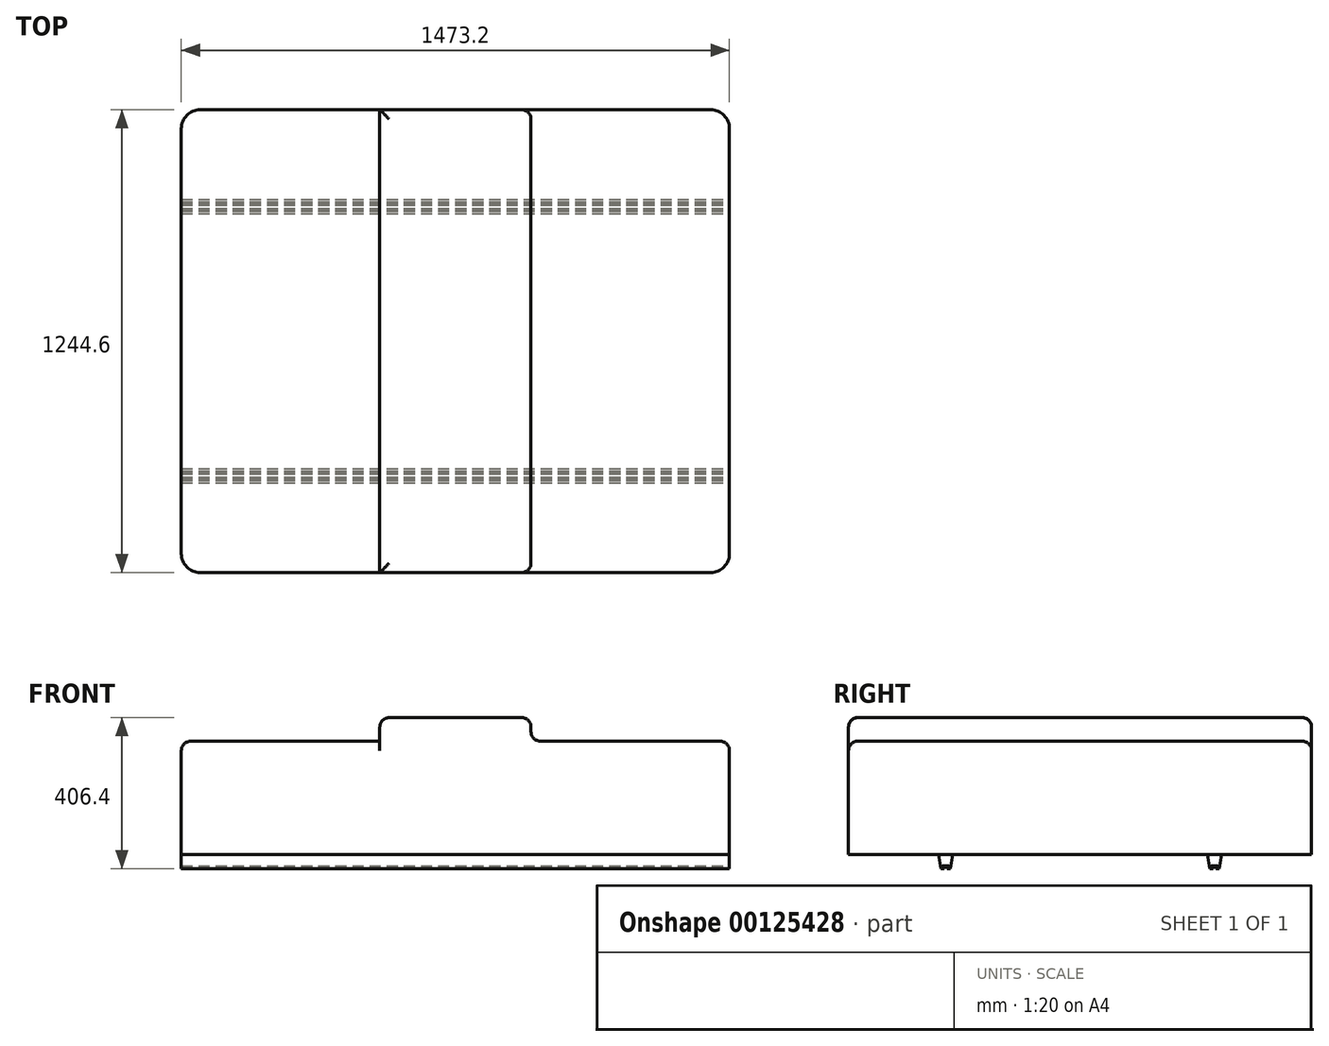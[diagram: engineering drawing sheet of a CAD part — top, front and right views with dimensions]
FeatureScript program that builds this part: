
annotation { "Feature Type Name" : "Feature", "Feature Type Description" : "" }
export const myFeature = defineFeature(function(context is Context, id is Id, definition is map)
    precondition{}
    {
        {
            var Q0;
            Q0=qCreatedBy(makeId("Top.planeOp"),FACE);
            var sketch = newSketch(context, id + "F0", { "sketchPlane" : qUnion([Q0])});
            skLineSegment(sketch, "E0.bottom", {"start": v(-736.6, -622.3) * mm, "end": v(736.6, -622.3) * mm});
            skLineSegment(sketch, "E0.top", {"start": v(-736.6, 622.3) * mm, "end": v(736.6, 622.3) * mm});
            skLineSegment(sketch, "E0.left", {"start": v(-736.6, -622.3) * mm, "end": v(-736.6, 622.3) * mm});
            skLineSegment(sketch, "E0.right", {"start": v(736.6, -622.3) * mm, "end": v(736.6, 622.3) * mm});
            skPoint(sketch, "E0.middle", {"position": v(0, 0) * mm});
            skSolve(sketch);
        }
        {
            var Q0;
            Q0 = qSketchRegion(id + "F0", true);
            var Q1;
            Q1=makeQuery(id+"F0.imprint","IMPRINT",FACE,{"disambiguationData":[TD([[makeQuery(id+"F0.imprint","IMPRINT",EDGE,{"derivedFrom":sQuery(id+"F0.wireOp",EDGE,"E0.bottom")}),1.0]])]});
            extrude(context, id + "F1", {"entities" : qUnion([Q0, Q1]), "depth" : 304.8 * mm});
        }
        {
            var Q0;
            Q0=makeQuery(id+"F1.opExtrude","CAP_FACE",FACE,{"disambiguationData":[OSD([sQuery(id+"F0.wireOp",EDGE,"E0.bottom"),sQuery(id+"F0.wireOp",EDGE,"E0.top"),sQuery(id+"F0.wireOp",EDGE,"E0.left"),sQuery(id+"F0.wireOp",EDGE,"E0.right")])],"isStart":false});
            var sketch = newSketch(context, id + "F2", { "sketchPlane" : qUnion([Q0])});
            skLineSegment(sketch, "E1", {"start": v(0, 622.3) * mm, "end": v(0, -622.3) * mm, "construction": true});
            skLineSegment(sketch, "E2.bottom", {"start": v(-203.2, 622.3) * mm, "end": v(203.2, 622.3) * mm});
            skLineSegment(sketch, "E2.top", {"start": v(-203.2, -622.3) * mm, "end": v(203.2, -622.3) * mm});
            skLineSegment(sketch, "E2.left", {"start": v(-203.2, 622.3) * mm, "end": v(-203.2, -622.3) * mm});
            skLineSegment(sketch, "E2.right", {"start": v(203.2, 622.3) * mm, "end": v(203.2, -622.3) * mm});
            skSolve(sketch);
        }
        {
            var Q0;
            Q0 = qSketchRegion(id + "F2", true);
            extrude(context, id + "F3", {"entities" : qUnion([Q0]), "operationType" : NewBodyOperationType.ADD, "depth" : 63.5 * mm});
        }
        {
            var Q0;
            Q0=makeQuery(id+"F3.opExtrude","CAP_EDGE",EDGE,{"disambiguationData":[OSD([sQuery(id+"F2.wireOp",EDGE,"E2.left")])],"isStart":true});
            var Q1;
            Q1=makeQuery(id+"F3.opExtrude","CAP_EDGE",EDGE,{"disambiguationData":[OSD([sQuery(id+"F2.wireOp",EDGE,"E2.left")])],"isStart":false});
            var Q2;
            Q2=makeQuery(id+"F3.opExtrude","CAP_EDGE",EDGE,{"disambiguationData":[OSD([sQuery(id+"F2.wireOp",EDGE,"E2.right")])],"isStart":false});
            var Q3;
            Q3=makeQuery(id+"F3.opExtrude","CAP_EDGE",EDGE,{"disambiguationData":[OSD([sQuery(id+"F2.wireOp",EDGE,"E2.right")])],"isStart":true});
            var Q4;
            Q4=makeQuery(id+"F3.opExtrude","CAP_EDGE",EDGE,{"disambiguationData":[OSD([sQuery(id+"F2.wireOp",EDGE,"E2.top")])],"isStart":false});
            var Q5;
            Q5=makeQuery(id+"F3.opExtrude","CAP_EDGE",EDGE,{"disambiguationData":[OSD([sQuery(id+"F2.wireOp",EDGE,"E2.bottom")])],"isStart":false});
            fillet(context, id + "F4", {"entities" : qUnion([Q0, Q1, Q2, Q3, Q4, Q5]), "radius" : 25.4 * mm, "tangentPropagation" : true, "allowEdgeOverflow" : false});
        }
        {
            var Q0;
            {var subQ0=sQuery(id+"F0.wireOp",EDGE,"E0.left");var subQ1=sQuery(id+"F0.wireOp",EDGE,"E0.bottom");Q0=makeQuery(id+"F3.boolean.opBoolean","SPLIT",EDGE,{"disambiguationData":[TD([makeQuery(id+"F1.opExtrude","SWEPT_FACE",FACE,{"disambiguationData":[OSD([subQ0])]})])],"derivedFrom":makeQuery(id+"F1.opExtrude","CAP_EDGE",EDGE,{"disambiguationData":[OSD([subQ1])],"isStart":false})});}
            var Q1;
            {var subQ0=sQuery(id+"F0.wireOp",EDGE,"E0.right");var subQ1=sQuery(id+"F0.wireOp",EDGE,"E0.bottom");Q1=makeQuery(id+"F3.boolean.opBoolean","SPLIT",EDGE,{"disambiguationData":[TD([makeQuery(id+"F1.opExtrude","SWEPT_FACE",FACE,{"disambiguationData":[OSD([subQ0])]})])],"derivedFrom":makeQuery(id+"F1.opExtrude","CAP_EDGE",EDGE,{"disambiguationData":[OSD([subQ1])],"isStart":false})});}
            var Q2;
            Q2=makeQuery(id+"F1.opExtrude","CAP_EDGE",EDGE,{"disambiguationData":[OSD([sQuery(id+"F0.wireOp",EDGE,"E0.right")])],"isStart":false});
            var Q3;
            {var subQ0=sQuery(id+"F0.wireOp",EDGE,"E0.right");var subQ1=sQuery(id+"F0.wireOp",EDGE,"E0.top");Q3=makeQuery(id+"F3.boolean.opBoolean","SPLIT",EDGE,{"disambiguationData":[TD([makeQuery(id+"F1.opExtrude","SWEPT_FACE",FACE,{"disambiguationData":[OSD([subQ0])]})])],"derivedFrom":makeQuery(id+"F1.opExtrude","CAP_EDGE",EDGE,{"disambiguationData":[OSD([subQ1])],"isStart":false})});}
            var Q4;
            {var subQ0=sQuery(id+"F0.wireOp",EDGE,"E0.left");var subQ1=sQuery(id+"F0.wireOp",EDGE,"E0.top");Q4=makeQuery(id+"F3.boolean.opBoolean","SPLIT",EDGE,{"disambiguationData":[TD([makeQuery(id+"F1.opExtrude","SWEPT_FACE",FACE,{"disambiguationData":[OSD([subQ0])]})])],"derivedFrom":makeQuery(id+"F1.opExtrude","CAP_EDGE",EDGE,{"disambiguationData":[OSD([subQ1])],"isStart":false})});}
            var Q5;
            Q5=makeQuery(id+"F1.opExtrude","CAP_EDGE",EDGE,{"disambiguationData":[OSD([sQuery(id+"F0.wireOp",EDGE,"E0.left")])],"isStart":false});
            fillet(context, id + "F5", {"entities" : qUnion([Q0, Q1, Q2, Q3, Q4, Q5]), "radius" : 25.4 * mm, "tangentPropagation" : true, "allowEdgeOverflow" : false});
        }
        {
            var Q0;
            Q0=makeQuery(id+"F1.opExtrude","SWEPT_EDGE",EDGE,{"disambiguationData":[OSD([sQuery(id+"F0.wireOp",EDGE,"E0.bottom"),sQuery(id+"F0.wireOp",EDGE,"E0.right")])]});
            var Q1;
            Q1=makeQuery(id+"F1.opExtrude","SWEPT_EDGE",EDGE,{"disambiguationData":[OSD([sQuery(id+"F0.wireOp",EDGE,"E0.top"),sQuery(id+"F0.wireOp",EDGE,"E0.right")])]});
            var Q2;
            Q2=makeQuery(id+"F1.opExtrude","SWEPT_EDGE",EDGE,{"disambiguationData":[OSD([sQuery(id+"F0.wireOp",EDGE,"E0.top"),sQuery(id+"F0.wireOp",EDGE,"E0.left")])]});
            var Q3;
            Q3=makeQuery(id+"F1.opExtrude","SWEPT_EDGE",EDGE,{"disambiguationData":[OSD([sQuery(id+"F0.wireOp",EDGE,"E0.bottom"),sQuery(id+"F0.wireOp",EDGE,"E0.left")])]});
            fillet(context, id + "F6", {"entities" : qUnion([Q0, Q1, Q2, Q3]), "radius" : 50.8 * mm, "tangentPropagation" : true, "allowEdgeOverflow" : false});
        }
        {
            var Q0;
            Q0=makeQuery(id+"F1.opExtrude","SWEPT_FACE",FACE,{"disambiguationData":[OSD([sQuery(id+"F0.wireOp",EDGE,"E0.right")])]});
            var sketch = newSketch(context, id + "F7", { "sketchPlane" : qUnion([Q0])});
            skLineSegment(sketch, "E3", {"start": v(0, 77.47) * mm, "end": v(0, -162.94) * mm, "construction": true});
            skLineSegment(sketch, "E4", {"start": v(-361.35, 0) * mm, "end": v(-361.35, -38.1) * mm, "construction": true});
            skLineSegment(sketch, "E5", {"start": v(-361.35, 0) * mm, "end": v(-342.3, 0) * mm});
            skLineSegment(sketch, "E6", {"start": v(-342.3, 0) * mm, "end": v(-348.66, -38.1) * mm});
            skLineSegment(sketch, "E7", {"start": v(-348.66, -38.1) * mm, "end": v(-357.05, -38.1) * mm});
            skLineSegment(sketch, "E8", {"start": v(-357.05, -38.1) * mm, "end": v(-357.05, -34.25) * mm});
            skLineSegment(sketch, "E9", {"start": v(-357.05, -34.25) * mm, "end": v(-352.06, -34.25) * mm});
            skLineSegment(sketch, "E10", {"start": v(-352.06, -34.25) * mm, "end": v(-352.06, -30.63) * mm});
            skLineSegment(sketch, "E11", {"start": v(-352.06, -30.63) * mm, "end": v(-361.35, -30.63) * mm});
            skLineSegment(sketch, "E12.MirrorCS", {"start": v(-361.35, 0) * mm, "end": v(-380.4, 0) * mm});
            skLineSegment(sketch, "E13.MirrorCS", {"start": v(-380.4, 0) * mm, "end": v(-374.04, -38.1) * mm});
            skLineSegment(sketch, "E14.MirrorCS", {"start": v(-374.04, -38.1) * mm, "end": v(-365.66, -38.1) * mm});
            skLineSegment(sketch, "E15.MirrorCS", {"start": v(-365.66, -38.1) * mm, "end": v(-365.66, -34.25) * mm});
            skLineSegment(sketch, "E16.MirrorCS", {"start": v(-365.66, -34.25) * mm, "end": v(-370.64, -34.25) * mm});
            skLineSegment(sketch, "E17.MirrorCS", {"start": v(-370.64, -34.25) * mm, "end": v(-370.64, -30.63) * mm});
            skLineSegment(sketch, "E18.MirrorCS", {"start": v(-370.64, -30.63) * mm, "end": v(-361.35, -30.63) * mm});
            skLineSegment(sketch, "E19.MirrorCS", {"start": v(365.66, -38.1) * mm, "end": v(365.66, -34.25) * mm});
            skLineSegment(sketch, "E20.MirrorCS", {"start": v(348.66, -38.1) * mm, "end": v(357.05, -38.1) * mm});
            skLineSegment(sketch, "E21.MirrorCS", {"start": v(357.05, -38.1) * mm, "end": v(357.05, -34.25) * mm});
            skLineSegment(sketch, "E22.MirrorCS", {"start": v(357.05, -34.25) * mm, "end": v(352.06, -34.25) * mm});
            skLineSegment(sketch, "E23.MirrorCS", {"start": v(352.06, -30.63) * mm, "end": v(361.35, -30.63) * mm});
            skLineSegment(sketch, "E24.MirrorCS", {"start": v(352.06, -34.25) * mm, "end": v(352.06, -30.63) * mm});
            skLineSegment(sketch, "E25.MirrorCS", {"start": v(370.64, -30.63) * mm, "end": v(361.35, -30.63) * mm});
            skLineSegment(sketch, "E26.MirrorCS", {"start": v(365.66, -34.25) * mm, "end": v(370.64, -34.25) * mm});
            skLineSegment(sketch, "E27.MirrorCS", {"start": v(361.35, 0) * mm, "end": v(342.3, 0) * mm});
            skLineSegment(sketch, "E28.MirrorCS", {"start": v(370.64, -34.25) * mm, "end": v(370.64, -30.63) * mm});
            skLineSegment(sketch, "E29.MirrorCS", {"start": v(374.04, -38.1) * mm, "end": v(365.66, -38.1) * mm});
            skLineSegment(sketch, "E30.MirrorCS", {"start": v(361.35, 0) * mm, "end": v(380.4, 0) * mm});
            skLineSegment(sketch, "E31.MirrorCS", {"start": v(361.35, 0) * mm, "end": v(361.35, -38.1) * mm, "construction": true});
            skLineSegment(sketch, "E32.MirrorCS", {"start": v(342.3, 0) * mm, "end": v(348.66, -38.1) * mm});
            skLineSegment(sketch, "E33.MirrorCS", {"start": v(380.4, 0) * mm, "end": v(374.04, -38.1) * mm});
            skSolve(sketch);
        }
        {
            var Q0;
            Q0=makeQuery(id+"F7.imprint","IMPRINT",FACE,{"disambiguationData":[TD([[makeQuery(id+"F7.imprint","IMPRINT",EDGE,{"derivedFrom":sQuery(id+"F7.wireOp",EDGE,"E5")}),-1.0]])]});
            var Q1;
            Q1=makeQuery(id+"F7.imprint","IMPRINT",FACE,{"disambiguationData":[TD([[makeQuery(id+"F7.imprint","IMPRINT",EDGE,{"derivedFrom":sQuery(id+"F7.wireOp",EDGE,"E19.MirrorCS")}),-1.0]])]});
            extrude(context, id + "F8", {"entities" : qUnion([Q0, Q1]), "oppositeDirection" : true, "depth" : 1473.2 * mm});
        }
    });
